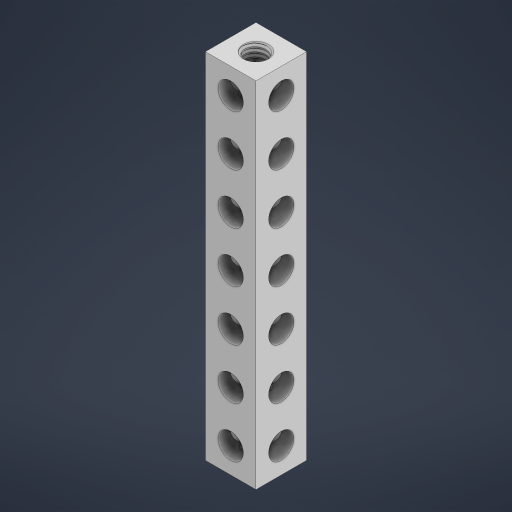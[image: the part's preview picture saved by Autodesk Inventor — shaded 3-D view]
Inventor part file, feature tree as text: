
AUTODESK INVENTOR PART (.ipt)
format: ipt  version: 2023 (Build 270158000, 158)  size: 1,362,944 bytes
history: native  units: in
note: dims shown in document units (in); Inventor stores cm internally (conversion verified against a paired STEP export)
features: mirror x1
ambient origin geometry x8: Origin, YZ Plane, XZ Plane, XY Plane, X Axis, Y Axis, Z Axis, Center Point
bodies: Solid1 (feature_tree)
feature tree (1):
  mirror  "Mirror3"
